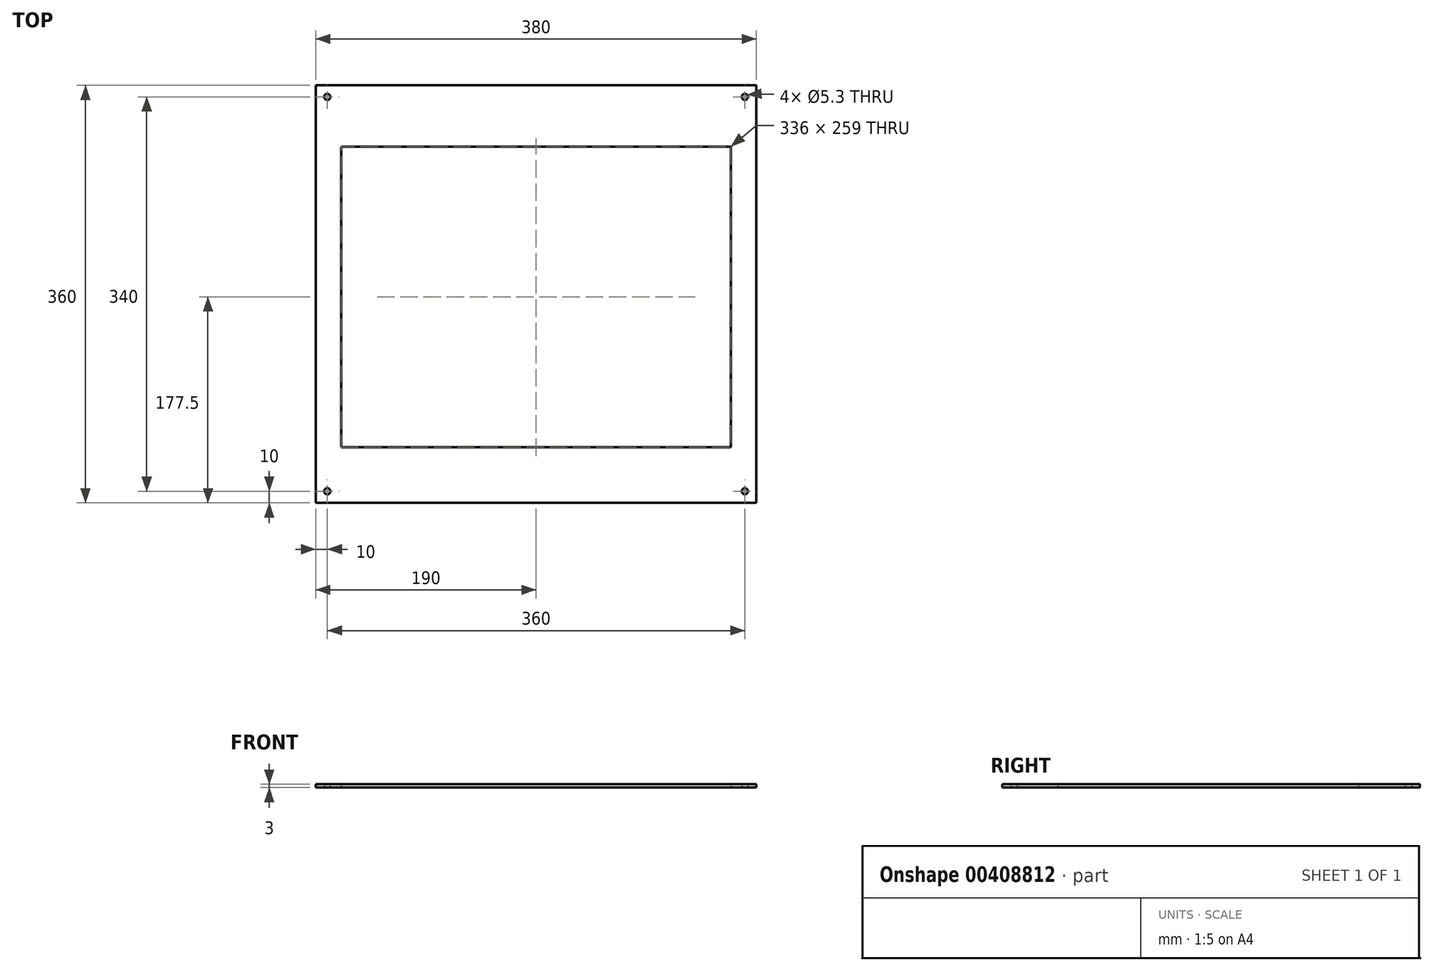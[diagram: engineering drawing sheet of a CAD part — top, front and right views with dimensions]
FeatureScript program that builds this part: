
annotation { "Feature Type Name" : "Feature", "Feature Type Description" : "" }
export const myFeature = defineFeature(function(context is Context, id is Id, definition is map)
    precondition{}
    {
        {
            var Q0;
            Q0=qCreatedBy(makeId("Top.planeOp"),FACE);
            var sketch = newSketch(context, id + "F0", { "sketchPlane" : qUnion([Q0])});
            skLineSegment(sketch, "E0.bottom", {"start": v(190, -180) * mm, "end": v(-190, -180) * mm});
            skLineSegment(sketch, "E0.top", {"start": v(190, 180) * mm, "end": v(-190, 180) * mm});
            skLineSegment(sketch, "E0.left", {"start": v(190, -180) * mm, "end": v(190, 180) * mm});
            skLineSegment(sketch, "E0.right", {"start": v(-190, -180) * mm, "end": v(-190, 180) * mm});
            skPoint(sketch, "E0.middle", {"position": v(0, 0) * mm});
            skLineSegment(sketch, "E1.bottom", {"start": v(168, -132) * mm, "end": v(-168, -132) * mm});
            skLineSegment(sketch, "E1.top", {"start": v(168, 127) * mm, "end": v(-168, 127) * mm});
            skLineSegment(sketch, "E1.left", {"start": v(168, -132) * mm, "end": v(168, 127) * mm});
            skLineSegment(sketch, "E1.right", {"start": v(-168, -132) * mm, "end": v(-168, 127) * mm});
            skCircle(sketch, "E2", {"center": v(-180, -170) * mm, "radius": 2.65 * mm});
            skCircle(sketch, "E3.MirrorC", {"center": v(180, -170) * mm, "radius": 2.65 * mm});
            skCircle(sketch, "E4.MirrorC", {"center": v(180, 170) * mm, "radius": 2.65 * mm});
            skCircle(sketch, "E5.MirrorC", {"center": v(-180, 170) * mm, "radius": 2.65 * mm});
            skSolve(sketch);
        }
        {
            var Q0;
            Q0=makeQuery(id+"F0.imprint","IMPRINT",FACE,{"disambiguationData":[TD([[makeQuery(id+"F0.imprint","IMPRINT",EDGE,{"derivedFrom":sQuery(id+"F0.wireOp",EDGE,"E0.bottom")}),-1.0]])]});
            extrude(context, id + "F1", {"entities" : qUnion([Q0]), "depth" : 3 * mm});
        }
    });
